# Revit family: ROSENBERG_EKA
name_source: partatom
category: Wyposażenie mechaniczne
revit_build: Autodesk Revit 2017 (Build: 20160225_1515(x64)
units: mm (PartAtom-declared; Revit-internal decimal feet)

## family parameters
Numer OmniClass = 23.75.00.00
Oparty na płaszczyźnie roboczej = Nie
Punkt obliczania pomieszczeń = Nie
Tnij formami wycięć po wczytaniu = Nie
Typ części = Dzieli na
Tytuł OmniClass = Climate Control (HVAC)
Współdzielony = Tak
Wymiar okrągłego złącza = Użyj średnicy
Zawsze pionowo = Tak

## types (36) — shared parameters
2R = 160 mm  [stored 0.524934 ft]
Date = 10.2018
Frequency = 50 Hz
Hole = 60 mm  [stored 0.19685 ft]
Materiał = <Wg kategorii>
Opis = Tube Fan
Producent = Rosenberg
R = 250 mm  [stored 0.82021 ft]
Ram = 180 mm  [stored 0.590551 ft]
URL = https://www.rosenberg.pl
Version = 1

## per-type parameters (varying)
| type | Air_flow | Current | FAN | Height | Height_connector | Length | Model | Power | Pressure | Protection Class | Voltage | Weight | Width | Width_2 | Width_connector |
| 200-4 Ex | 0.0 m³/h | 1 A | 240 mm  [stored 0.787402 ft] | 200 mm  [stored 0.656168 ft] | 200 mm  [stored 0.656168 ft] | 445 mm  [stored 1.45997 ft] | 200-4 Ex | 290 W | 0.0 Pa | IP44 | 400 V | 12.30 kg | 400 mm  [stored 1.31234 ft] | 440 mm  [stored 1.44357 ft] | 400 mm  [stored 1.31234 ft] |
| 225-4 Zone 1 | 0.0 m³/h | 1 A | 290 mm | 250 mm  [stored 0.82021 ft] | 250 mm  [stored 0.82021 ft] | 530 mm  [stored 1.73885 ft] | 225-4 Zone 1 | 540 W | 0.0 Pa | IP44 | 400 V | 19.00 kg | 500 mm  [stored 1.64042 ft] | 540 mm  [stored 1.77165 ft] | 500 mm  [stored 1.64042 ft] |
| 250-4 Zone 1 | 0.0 m³/h | 1 A | 340 mm  [stored 1.11549 ft] | 300 mm | 300 mm | 560 mm  [stored 1.83727 ft] | 250-4 Zone 1 | 750 W | 0.0 Pa | IP44 | 400 V | 22.50 kg | 500 mm  [stored 1.64042 ft] | 540 mm  [stored 1.77165 ft] | 500 mm  [stored 1.64042 ft] |
| 280-4 Zone 1 | 0.0 m³/h | 3 A | 340 mm  [stored 1.11549 ft] | 300 mm | 300 mm | 680 mm  [stored 2.23097 ft] | 280-4 Zone 1 | 1500 W | 0.0 Pa | IP44 | 400 V | 26.50 kg | 600 mm | 640 mm  [stored 2.09974 ft] | 600 mm |
| 280-6 Zone 1 | 0.0 m³/h | 1 A | 340 mm  [stored 1.11549 ft] | 300 mm | 300 mm | 680 mm  [stored 2.23097 ft] | 280-6 Zone 1 | 530 W | 0.0 Pa | IP44 | 400 V | 28.00 kg | 600 mm | 640 mm  [stored 2.09974 ft] | 600 mm |
| 315-4 Zone 1 | 0.0 m³/h | 4 A | 390 mm  [stored 1.27953 ft] | 350 mm  [stored 1.14829 ft] | 350 mm  [stored 1.14829 ft] | 700 mm  [stored 2.29659 ft] | 315-4 Zone 1 | 2000 W | 0.0 Pa | IP44 | 400 V | 44.50 kg | 600 mm | 640 mm  [stored 2.09974 ft] | 600 mm |
| 315-6 Zone 1 | 0.0 m³/h | 1 A | 390 mm  [stored 1.27953 ft] | 350 mm  [stored 1.14829 ft] | 350 mm  [stored 1.14829 ft] | 700 mm  [stored 2.29659 ft] | 315-6 Zone 1 | 710 W | 0.0 Pa | IP44 | 400 V | 37.50 kg | 600 mm | 640 mm  [stored 2.09974 ft] | 600 mm |
| 355-6 Zone 1 | 0.0 m³/h | 2 A | 440 mm  [stored 1.44357 ft] | 400 mm  [stored 1.31234 ft] | 400 mm  [stored 1.31234 ft] | 780 mm  [stored 2.55906 ft] | 355-6 Zone 1 | 1350 W | 0.0 Pa | IP44 | 400 V | 51.00 kg | 700 mm  [stored 2.29659 ft] | 740 mm  [stored 2.42782 ft] | 700 mm  [stored 2.29659 ft] |
| 280-4.6FA | 1482.0 m³/h | 2 A | 340 mm  [stored 1.11549 ft] | 300 mm | 300 mm | 680 mm  [stored 2.23097 ft] | 280-4.6FA | 1090 W | 438.0 Pa | IP54 | 400 V | 35.00 kg | 600 mm | 640 mm  [stored 2.09974 ft] | 600 mm |
| 315-4.6HF_400V | 1849.0 m³/h | 4 A | 390 mm  [stored 1.27953 ft] | 350 mm  [stored 1.14829 ft] | 350 mm  [stored 1.14829 ft] | 700 mm  [stored 2.29659 ft] | 315-4.6HF | 1950 W | 616.0 Pa | IP54 | 400 V | 44.00 kg | 600 mm | 640 mm  [stored 2.09974 ft] | 600 mm |
| 400-6.7KF_400V | 3455.0 m³/h | 5 A | 540 mm  [stored 1.77165 ft] | 500 mm  [stored 1.64042 ft] | 500 mm  [stored 1.64042 ft] | 880 mm  [stored 2.88714 ft] | 400-6.7KF | 2750 W | 489.0 Pa | IP54 | 400 V | 82.00 kg | 800 mm  [stored 2.62467 ft] | 840 mm  [stored 2.75591 ft] | 800 mm  [stored 2.62467 ft] |
| 400-8.7HA | 2213.0 m³/h | 3 A | 540 mm  [stored 1.77165 ft] | 500 mm  [stored 1.64042 ft] | 500 mm  [stored 1.64042 ft] | 880 mm  [stored 2.88714 ft] | 400-8.7HA | 1400 W | 290.0 Pa | IP54 | 400 V | 75.00 kg | 800 mm  [stored 2.62467 ft] | 840 mm  [stored 2.75591 ft] | 800 mm  [stored 2.62467 ft] |
| 450-6.7NA_400V | 4830.0 m³/h | 7 A | 540 mm  [stored 1.77165 ft] | 500 mm  [stored 1.64042 ft] | 500 mm  [stored 1.64042 ft] | 1035 mm  [stored 3.39567 ft] | 450-6.7NA | 3350 W | 588.0 Pa | IP54 | 400 V | 97.00 kg | 900 mm  [stored 2.95276 ft] | 940 mm  [stored 3.08399 ft] | 900 mm  [stored 2.95276 ft] |
| 450-8.7KF_400V | 4566.0 m³/h | 4 A | 540 mm  [stored 1.77165 ft] | 500 mm  [stored 1.64042 ft] | 500 mm  [stored 1.64042 ft] | 1035 mm  [stored 3.39567 ft] | EKAD 450-8.7KF | 1930 W | 339.0 Pa | IP54 | 400 V | 85.00 kg | 900 mm  [stored 2.95276 ft] | 940 mm  [stored 3.08399 ft] | 900 mm  [stored 2.95276 ft] |
| 355-4.7KF_400V | 3752.0 m³/h | 6 A | 440 mm  [stored 1.44357 ft] | 400 mm  [stored 1.31234 ft] | 400 mm  [stored 1.31234 ft] | 780 mm  [stored 2.55906 ft] | 355-4.7KF | 3350 W | 810.0 Pa | IP54 | 400 V | 61.00 kg | 700 mm  [stored 2.29659 ft] | 740 mm  [stored 2.42782 ft] | 700 mm  [stored 2.29659 ft] |
| 200-2_230V | 592.0 m³/h | 1 A | 240 mm  [stored 0.787402 ft] | 200 mm  [stored 0.656168 ft] | 200 mm  [stored 0.656168 ft] | 445 mm  [stored 1.45997 ft] | 200-2 | 170 W | 325.0 Pa | IP44 | 230 V | 12.00 kg | 400 mm  [stored 1.31234 ft] | 440 mm  [stored 1.44357 ft] | 400 mm  [stored 1.31234 ft] |
| 200-4_230V | 732.0 m³/h | 1 A | 240 mm  [stored 0.787402 ft] | 200 mm  [stored 0.656168 ft] | 200 mm  [stored 0.656168 ft] | 445 mm  [stored 1.45997 ft] | 200-4 | 290 W | 223.0 Pa | IP54 | 230 V | 12.00 kg | 400 mm  [stored 1.31234 ft] | 440 mm  [stored 1.44357 ft] | 400 mm  [stored 1.31234 ft] |
| 225-4_230V | 957.0 m³/h | 2 A | 290 mm | 250 mm  [stored 0.82021 ft] | 250 mm  [stored 0.82021 ft] | 530 mm  [stored 1.73885 ft] | 225-4 | 490 W | 306.0 Pa | IP54 | 230 V | 18.00 kg | 500 mm  [stored 1.64042 ft] | 540 mm  [stored 1.77165 ft] | 500 mm  [stored 1.64042 ft] |
| 225-4 K_230V | 821.0 m³/h | 2 A | 290 mm | 250 mm  [stored 0.82021 ft] | 250 mm  [stored 0.82021 ft] | 530 mm  [stored 1.73885 ft] | 225-4 K | 360 W | 222.0 Pa | IP54 | 230 V | 17.00 kg | 500 mm  [stored 1.64042 ft] | 540 mm  [stored 1.77165 ft] | 500 mm  [stored 1.64042 ft] |
| 250-4_230V | 1232.0 m³/h | 3 A | 340 mm  [stored 1.11549 ft] | 300 mm | 300 mm | 560 mm  [stored 1.83727 ft] | 250-4 | 730 W | 328.0 Pa | IP54 | 230 V | 17.00 kg | 500 mm  [stored 1.64042 ft] | 540 mm  [stored 1.77165 ft] | 500 mm  [stored 1.64042 ft] |
| 250-4.5FA_230V | 1272.0 m³/h | 3 A | 340 mm  [stored 1.11549 ft] | 300 mm | 300 mm | 560 mm  [stored 1.83727 ft] | 250-4.5FA | 620 W | 367.0 Pa | IP54 | 400 V | 23.00 kg | 500 mm  [stored 1.64042 ft] | 540 mm  [stored 1.77165 ft] | 500 mm  [stored 1.64042 ft] |
| 250-6_230V | 960.0 m³/h | 1 A | 340 mm  [stored 1.11549 ft] | 300 mm | 300 mm | 560 mm  [stored 1.83727 ft] | 250-6 | 320 W | 154.0 Pa | IP54 | 230 V | 24.50 kg | 500 mm  [stored 1.64042 ft] | 540 mm  [stored 1.77165 ft] | 500 mm  [stored 1.64042 ft] |
| 280-4_230V | 1840.0 m³/h | 6 A | 340 mm  [stored 1.11549 ft] | 300 mm | 300 mm | 680 mm  [stored 2.23097 ft] | 280-4 | 1250 W | 438.0 Pa | IP54 | 230 V | 39.00 kg | 600 mm | 640 mm  [stored 2.09974 ft] | 600 mm |
| 280-4.6FA_230V | 1768.0 m³/h | 6 A | 340 mm  [stored 1.11549 ft] | 300 mm | 300 mm | 680 mm  [stored 2.23097 ft] | 280-4.6FA | 1160 W | 437.0 Pa | IP54 | 230 V | 39.00 kg | 600 mm | 640 mm  [stored 2.09974 ft] | 600 mm |
| 280-6 K_230V | 1269.0 m³/h | 2 A | 340 mm  [stored 1.11549 ft] | 300 mm | 300 mm | 680 mm  [stored 2.23097 ft] | 280-6 K | 380 W | 205.0 Pa | IP54 | 230 V | 25.50 kg | 600 mm | 640 mm  [stored 2.09974 ft] | 600 mm |
| 315-6 K_230V | 1791.0 m³/h | 3 A | 390 mm  [stored 1.27953 ft] | 350 mm  [stored 1.14829 ft] | 350 mm  [stored 1.14829 ft] | 700 mm  [stored 2.29659 ft] | 315-6 K | 720 W | 243.0 Pa | IP54 | 230 V | 34.00 kg | 600 mm | 640 mm  [stored 2.09974 ft] | 600 mm |
| 200-4_400V | 413.0 m³/h | 1 A | 240 mm  [stored 0.787402 ft] | 200 mm  [stored 0.656168 ft] | 200 mm  [stored 0.656168 ft] | 445 mm  [stored 1.45997 ft] | 200-4 | 330 W | 192.0 Pa | IP54 | 400 V | 12.00 kg | 400 mm  [stored 1.31234 ft] | 440 mm  [stored 1.44357 ft] | 400 mm  [stored 1.31234 ft] |
| 225-4 K_400V | 688.0 m³/h | 1 A | 290 mm | 250 mm  [stored 0.82021 ft] | 250 mm  [stored 0.82021 ft] | 530 mm  [stored 1.73885 ft] | 225-4 K | 410 W | 265.0 Pa | IP54 | 400 V | 16.00 kg | 500 mm  [stored 1.64042 ft] | 540 mm  [stored 1.77165 ft] | 500 mm  [stored 1.64042 ft] |
| 250-4_400V | 1204.0 m³/h | 2 A | 340 mm  [stored 1.11549 ft] | 300 mm | 300 mm | 560 mm  [stored 1.83727 ft] | 250-4 | 830 W | 347.0 Pa | IP54 | 400 V | 26.00 kg | 500 mm  [stored 1.64042 ft] | 540 mm  [stored 1.77165 ft] | 500 mm  [stored 1.64042 ft] |
| 250-4.5FA_400V | 1108.0 m³/h | 1 A | 340 mm  [stored 1.11549 ft] | 300 mm | 300 mm | 560 mm  [stored 1.83727 ft] | 250-4.5FA | 760 W | 367.0 Pa | IP54 | 400 V | 26.00 kg | 500 mm  [stored 1.64042 ft] | 540 mm  [stored 1.77165 ft] | 500 mm  [stored 1.64042 ft] |
| 280-4_400V | 1295.0 m³/h | 3 A | 340 mm  [stored 1.11549 ft] | 300 mm | 300 mm | 680 mm  [stored 2.23097 ft] | 280-4 | 1400 W | 422.0 Pa | IP54 | 400 V | 26.00 kg | 600 mm | 640 mm  [stored 2.09974 ft] | 600 mm |
| 280-4 K_400V | 1512.0 m³/h | 2 A | 340 mm  [stored 1.11549 ft] | 300 mm | 300 mm | 680 mm  [stored 2.23097 ft] | 280-4 K | 1100 W | 433.0 Pa | IP54 | 400 V | 26.00 kg | 600 mm | 640 mm  [stored 2.09974 ft] | 600 mm |
| 280-6_400V | 1297.0 m³/h | 1 A | 340 mm  [stored 1.11549 ft] | 300 mm | 300 mm | 680 mm  [stored 2.23097 ft] | 280-6 | 430 W | 200.0 Pa | IP54 | 400 V | 28.50 kg | 600 mm | 640 mm  [stored 2.09974 ft] | 600 mm |
| 315-6_400V | 1709.0 m³/h | 2 A | 390 mm  [stored 1.27953 ft] | 350 mm  [stored 1.14829 ft] | 350 mm  [stored 1.14829 ft] | 700 mm  [stored 2.29659 ft] | 315-6 | 820 W | 252.0 Pa | IP54 | 400 V | 46.50 kg | 600 mm | 640 mm  [stored 2.09974 ft] | 600 mm |
| 355-4_400V | 2292.0 m³/h | 6 A | 440 mm  [stored 1.44357 ft] | 400 mm  [stored 1.31234 ft] | 400 mm  [stored 1.31234 ft] | 780 mm  [stored 2.55906 ft] | 355-4 | 3200 W | 596.0 Pa | IP54 | 400 V | 46.50 kg | 700 mm  [stored 2.29659 ft] | 740 mm  [stored 2.42782 ft] | 700 mm  [stored 2.29659 ft] |
| 355-6 K_400V | 2268.0 m³/h | 2 A | 440 mm  [stored 1.44357 ft] | 400 mm  [stored 1.31234 ft] | 400 mm  [stored 1.31234 ft] | 780 mm  [stored 2.55906 ft] | 355-6 K | 1150 W | 321.0 Pa | IP54 | 400 V | 55.50 kg | 700 mm  [stored 2.29659 ft] | 740 mm  [stored 2.42782 ft] | 700 mm  [stored 2.29659 ft] |

note: [stored X ft] marks values corroborated as IEEE doubles in the binary element streams (Revit-internal decimal feet)

## geometry (parser evidence)
native form markers: Blend x4, Sweep x5
no freeform markers — native parametric forms only
